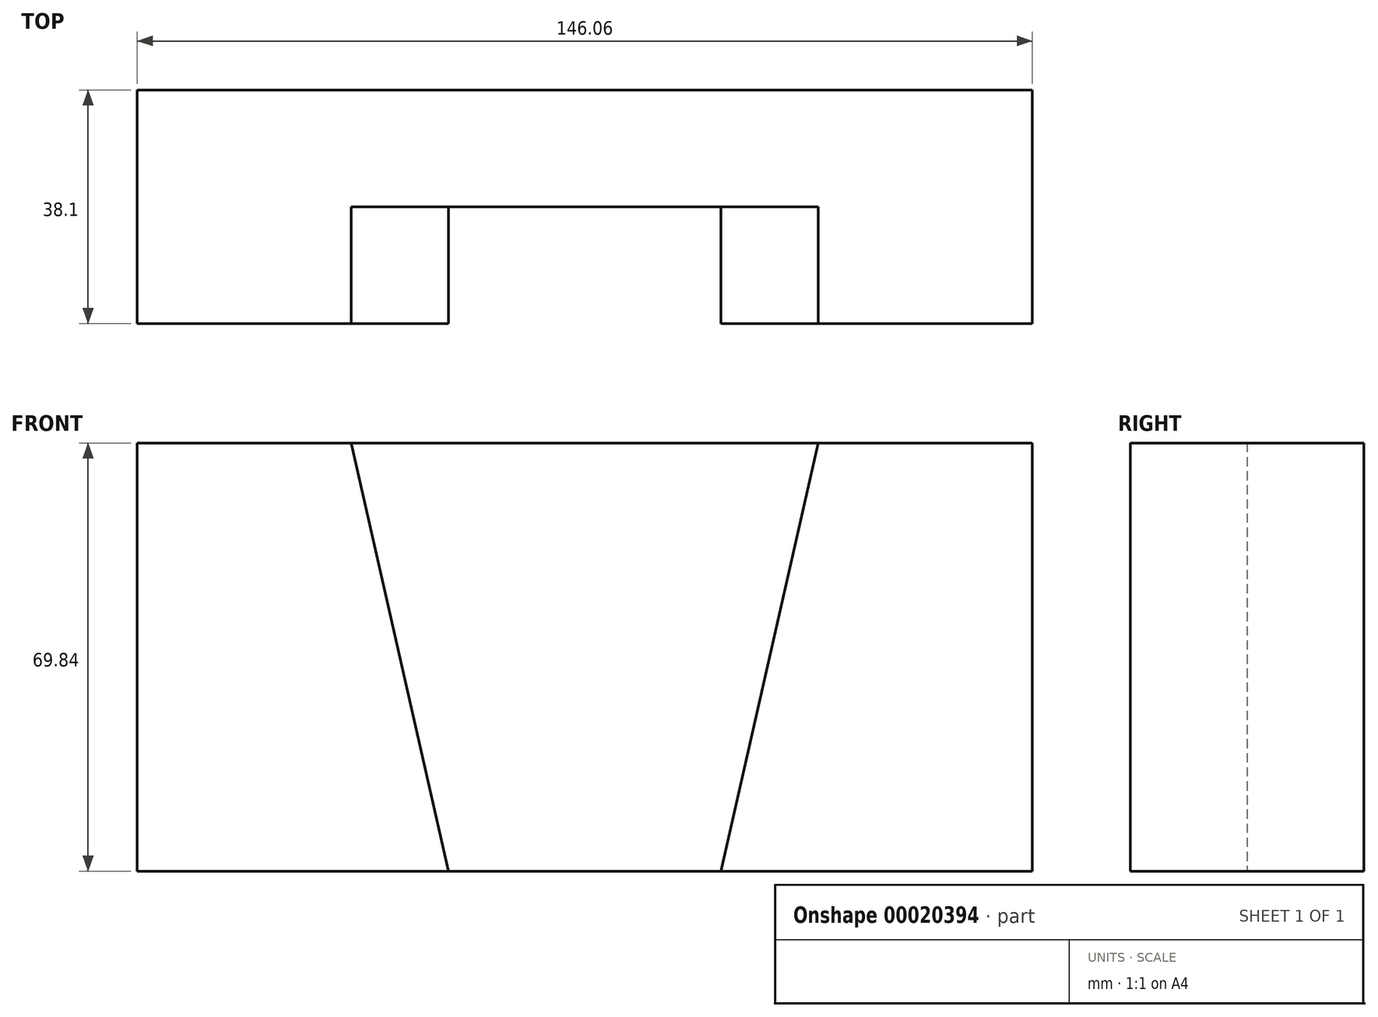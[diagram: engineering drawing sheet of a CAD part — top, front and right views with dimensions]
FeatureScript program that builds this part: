
annotation { "Feature Type Name" : "Feature", "Feature Type Description" : "" }
export const myFeature = defineFeature(function(context is Context, id is Id, definition is map)
    precondition{}
    {
        {
            var Q0;
            Q0=qCreatedBy(makeId("Front.planeOp"),FACE);
            var sketch = newSketch(context, id + "F0", { "sketchPlane" : qUnion([Q0])});
            skLineSegment(sketch, "E0.rect.bottom", {"start": v(-73.02, 34.92) * mm, "end": v(73.03, 34.92) * mm});
            skLineSegment(sketch, "E0.rect.top", {"start": v(-73.03, -34.92) * mm, "end": v(73.02, -34.92) * mm});
            skLineSegment(sketch, "E0.rect.left", {"start": v(-73.03, 34.92) * mm, "end": v(-73.03, -34.92) * mm});
            skLineSegment(sketch, "E0.rect.right", {"start": v(73.03, 34.92) * mm, "end": v(73.02, -34.92) * mm});
            skPoint(sketch, "E0.rect.middle", {"position": v(0, 0) * mm});
            skSolve(sketch);
        }
        {
            var Q0;
            Q0 = qSketchRegion(id + "F0", true);
            var Q1;
            Q1=makeQuery(id+"F0.imprint","IMPRINT",FACE,{"disambiguationData":[TD([[makeQuery(id+"F0.imprint","IMPRINT",EDGE,{"derivedFrom":sQuery(id+"F0.wireOp",EDGE,"E0.rect.bottom")}),-1.0]])]});
            extrude(context, id + "F1", {"entities" : qUnion([Q0, Q1]), "depth" : 38.1 * mm});
        }
        {
            var Q0;
            Q0=makeQuery(id+"F1.opExtrude","CAP_FACE",FACE,{"disambiguationData":[OSD([sQuery(id+"F0.wireOp",EDGE,"E0.rect.bottom"),sQuery(id+"F0.wireOp",EDGE,"E0.rect.top"),sQuery(id+"F0.wireOp",EDGE,"E0.rect.left"),sQuery(id+"F0.wireOp",EDGE,"E0.rect.right")])],"isStart":false});
            var sketch = newSketch(context, id + "F2", { "sketchPlane" : qUnion([Q0])});
            skLineSegment(sketch, "E1", {"start": v(-38.1, 34.93) * mm, "end": v(-22.23, -34.93) * mm});
            skLineSegment(sketch, "E2.MirrorCS", {"start": v(38.1, 34.93) * mm, "end": v(22.22, -34.93) * mm});
            skPoint(sketch, "E3.end.orphan", {"position": v(0, -34.92) * mm});
            skPoint(sketch, "E3.start.orphan", {"position": v(0, 34.92) * mm});
            skSolve(sketch);
        }
        {
            var Q0;
            {var subQ2=sQuery(id+"F2.wireOp",EDGE,"E1");Q0=makeQuery(id+"F2.imprint","IMPRINT",FACE,{"disambiguationData":[TD([[makeQuery(id+"F2.imprint","IMPRINT",EDGE,{"derivedFrom":subQ2}),1.0]])]});}
            extrude(context, id + "F3", {"entities" : qUnion([Q0]), "operationType" : NewBodyOperationType.REMOVE, "oppositeDirection" : true, "depth" : 19.05 * mm});
        }
    });
